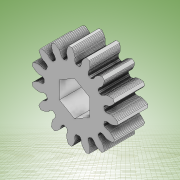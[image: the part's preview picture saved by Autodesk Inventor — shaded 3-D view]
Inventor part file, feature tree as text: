
AUTODESK INVENTOR PART (.ipt)
format: ipt  version: 2022 (Build 260153000, 153)  size: 1,219,584 bytes
history: native  units: mm
features: other x1, extrude x1, sketch x1
ambient origin geometry x8: Origin, YZ Plane, XZ Plane, XY Plane, X Axis, Y Axis, Z Axis, Center Point
bodies: Body1 (feature_tree)
feature tree (3):
  other  "Sólido1"
  extrude  "Extrusión1"  Depth=6.0mm TaperAngle=0.0deg
  sketch  "Boceto1"  dims[d0=6.0mm d1=6.0mm d2=0.0mm]
